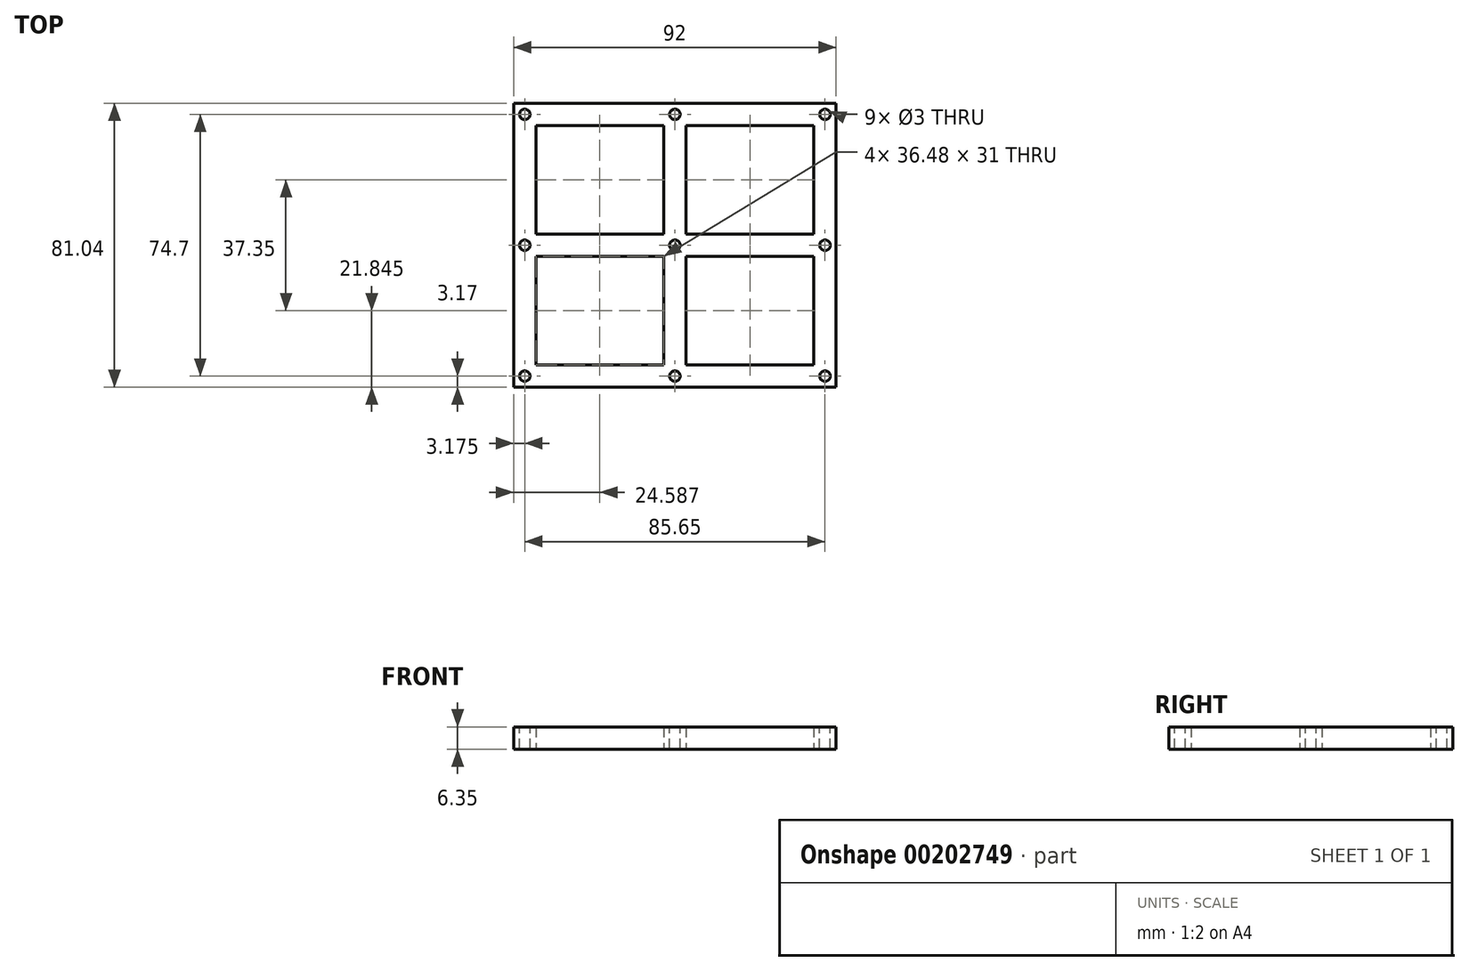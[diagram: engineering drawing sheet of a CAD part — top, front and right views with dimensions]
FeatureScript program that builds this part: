
annotation { "Feature Type Name" : "Feature", "Feature Type Description" : "" }
export const myFeature = defineFeature(function(context is Context, id is Id, definition is map)
    precondition{}
    {
        {
            var Q0;
            Q0=qCreatedBy(makeId("Top.planeOp"),FACE);
            var sketch = newSketch(context, id + "F0", { "sketchPlane" : qUnion([Q0])});
            skLineSegment(sketch, "E0.bottom", {"start": v(46, -40.52) * mm, "end": v(-46, -40.53) * mm});
            skLineSegment(sketch, "E0.top", {"start": v(46, 40.53) * mm, "end": v(-46, 40.52) * mm});
            skLineSegment(sketch, "E0.left", {"start": v(46, -40.52) * mm, "end": v(46, 40.53) * mm});
            skLineSegment(sketch, "E0.right", {"start": v(-46, -40.53) * mm, "end": v(-46, 40.52) * mm});
            skPoint(sketch, "E0.middle", {"position": v(0, 0) * mm});
            skSolve(sketch);
        }
        {
            var Q0;
            Q0 = qSketchRegion(id + "F0", true);
            extrude(context, id + "F1", {"entities" : qUnion([Q0]), "depth" : 6.35 * mm});
        }
        {
            var Q0;
            Q0=makeQuery(id+"F1.opExtrude","CAP_FACE",FACE,{"disambiguationData":[OSD([sQuery(id+"F0.wireOp",EDGE,"E0.bottom"),sQuery(id+"F0.wireOp",EDGE,"E0.top"),sQuery(id+"F0.wireOp",EDGE,"E0.left"),sQuery(id+"F0.wireOp",EDGE,"E0.right")])],"isStart":false});
            var sketch = newSketch(context, id + "F2", { "sketchPlane" : qUnion([Q0])});
            skLineSegment(sketch, "E1.bottom", {"start": v(46, 40.53) * mm, "end": v(39.65, 40.53) * mm});
            skLineSegment(sketch, "E1.top", {"start": v(46, 34.18) * mm, "end": v(39.65, 34.18) * mm});
            skLineSegment(sketch, "E1.left", {"start": v(46, 40.53) * mm, "end": v(46, 34.18) * mm});
            skLineSegment(sketch, "E1.right", {"start": v(39.65, 40.53) * mm, "end": v(39.65, 34.18) * mm});
            skLineSegment(sketch, "E2.bottom", {"start": v(-46, -40.53) * mm, "end": v(-39.65, -40.53) * mm});
            skLineSegment(sketch, "E2.top", {"start": v(-46, -34.18) * mm, "end": v(-39.65, -34.18) * mm});
            skLineSegment(sketch, "E2.left", {"start": v(-46, -40.53) * mm, "end": v(-46, -34.18) * mm});
            skLineSegment(sketch, "E2.right", {"start": v(-39.65, -40.53) * mm, "end": v(-39.65, -34.18) * mm});
            skLineSegment(sketch, "E3.bottom", {"start": v(46, -40.52) * mm, "end": v(39.65, -40.52) * mm});
            skLineSegment(sketch, "E3.top", {"start": v(46, -34.18) * mm, "end": v(39.65, -34.18) * mm});
            skLineSegment(sketch, "E3.left", {"start": v(46, -40.52) * mm, "end": v(46, -34.18) * mm});
            skLineSegment(sketch, "E3.right", {"start": v(39.65, -40.52) * mm, "end": v(39.65, -34.18) * mm});
            skLineSegment(sketch, "E4.bottom", {"start": v(46, -3.17) * mm, "end": v(39.65, -3.17) * mm});
            skLineSegment(sketch, "E4.top", {"start": v(46, 3.17) * mm, "end": v(39.65, 3.17) * mm});
            skLineSegment(sketch, "E4.left", {"start": v(46, -3.17) * mm, "end": v(46, 3.17) * mm});
            skLineSegment(sketch, "E4.right", {"start": v(-46, -3.17) * mm, "end": v(-46, 3.17) * mm});
            skPoint(sketch, "E4.middle", {"position": v(0, 0) * mm});
            skLineSegment(sketch, "E5.left", {"start": v(46, 3.17) * mm, "end": v(46, -3.17) * mm});
            skLineSegment(sketch, "E5.right", {"start": v(39.65, 3.17) * mm, "end": v(39.65, -3.17) * mm});
            skLineSegment(sketch, "E6.bottom", {"start": v(-46, 3.17) * mm, "end": v(-39.65, 3.17) * mm});
            skLineSegment(sketch, "E6.top", {"start": v(-46, -3.17) * mm, "end": v(-39.65, -3.17) * mm});
            skLineSegment(sketch, "E6.left", {"start": v(-46, 3.17) * mm, "end": v(-46, -3.17) * mm});
            skLineSegment(sketch, "E6.right", {"start": v(-39.65, 3.17) * mm, "end": v(-39.65, -3.17) * mm});
            skLineSegment(sketch, "E7.trimOffspring", {"start": v(-39.65, 3.17) * mm, "end": v(-46, 3.17) * mm});
            skLineSegment(sketch, "E8.trimOffspring", {"start": v(-39.65, -3.17) * mm, "end": v(-46, -3.17) * mm});
            skLineSegment(sketch, "E9.bottom", {"start": v(-46, 40.52) * mm, "end": v(-39.65, 40.52) * mm});
            skLineSegment(sketch, "E9.top", {"start": v(-46, 34.17) * mm, "end": v(-39.65, 34.17) * mm});
            skLineSegment(sketch, "E9.left", {"start": v(-46, 40.52) * mm, "end": v(-46, 34.17) * mm});
            skLineSegment(sketch, "E9.right", {"start": v(-39.65, 40.52) * mm, "end": v(-39.65, 34.17) * mm});
            skPoint(sketch, "E10", {"position": v(-42.83, 37.35) * mm});
            skPoint(sketch, "E10.positionSnap0", {"position": v(-46, 37.35) * mm});
            skPoint(sketch, "E10.positionSnap1", {"position": v(-42.83, 40.52) * mm});
            skPoint(sketch, "E11.positionSnap1", {"position": v(0, 40.53) * mm});
            skPoint(sketch, "E12", {"position": v(42.82, 37.35) * mm});
            skPoint(sketch, "E12.positionSnap0", {"position": v(39.65, 37.35) * mm});
            skPoint(sketch, "E12.positionSnap1", {"position": v(42.82, 40.53) * mm});
            skPoint(sketch, "E13", {"position": v(-42.83, 0) * mm});
            skPoint(sketch, "E13.positionSnap0", {"position": v(-46, 0) * mm});
            skPoint(sketch, "E13.positionSnap1", {"position": v(-42.83, 3.17) * mm});
            skPoint(sketch, "E14", {"position": v(-42.82, -37.35) * mm});
            skPoint(sketch, "E14.positionSnap0", {"position": v(-46, -37.35) * mm});
            skPoint(sketch, "E14.positionSnap1", {"position": v(-42.82, -34.18) * mm});
            skPoint(sketch, "E15", {"position": v(42.83, 0) * mm});
            skPoint(sketch, "E15.positionSnap0", {"position": v(42.83, 3.17) * mm});
            skPoint(sketch, "E15.positionSnap1", {"position": v(46, 0) * mm});
            skPoint(sketch, "E16", {"position": v(42.83, -37.35) * mm});
            skPoint(sketch, "E16.positionSnap0", {"position": v(39.65, -37.35) * mm});
            skPoint(sketch, "E16.positionSnap1", {"position": v(42.83, -34.18) * mm});
            skPoint(sketch, "E17", {"position": v(0, 37.35) * mm});
            skLineSegment(sketch, "E18.bottom", {"start": v(3.17, 40.53) * mm, "end": v(-3.18, 40.53) * mm});
            skLineSegment(sketch, "E18.top", {"start": v(3.17, 34.18) * mm, "end": v(-3.18, 34.18) * mm});
            skLineSegment(sketch, "E18.left", {"start": v(3.17, 40.53) * mm, "end": v(3.17, 34.18) * mm});
            skLineSegment(sketch, "E18.right", {"start": v(-3.18, 40.53) * mm, "end": v(-3.18, 34.18) * mm});
            skLineSegment(sketch, "E19.bottom", {"start": v(3.18, -3.17) * mm, "end": v(-3.17, -3.18) * mm});
            skLineSegment(sketch, "E19.top", {"start": v(3.17, 3.18) * mm, "end": v(-3.18, 3.17) * mm});
            skLineSegment(sketch, "E19.left", {"start": v(3.18, -3.17) * mm, "end": v(3.17, 3.18) * mm});
            skLineSegment(sketch, "E19.right", {"start": v(-3.17, -3.18) * mm, "end": v(-3.18, 3.17) * mm});
            skPoint(sketch, "E20", {"position": v(0, -37.35) * mm});
            skLineSegment(sketch, "E21.bottom", {"start": v(3.18, -40.53) * mm, "end": v(-3.17, -40.53) * mm});
            skLineSegment(sketch, "E21.top", {"start": v(3.18, -34.18) * mm, "end": v(-3.17, -34.18) * mm});
            skLineSegment(sketch, "E21.left", {"start": v(3.18, -40.53) * mm, "end": v(3.18, -34.18) * mm});
            skLineSegment(sketch, "E21.right", {"start": v(-3.17, -40.53) * mm, "end": v(-3.17, -34.18) * mm});
            skSolve(sketch);
        }
        {
            var Q0;
            Q0=makeQuery(id+"F1.opExtrude","CAP_FACE",FACE,{"disambiguationData":[OSD([sQuery(id+"F0.wireOp",EDGE,"E0.bottom"),sQuery(id+"F0.wireOp",EDGE,"E0.top"),sQuery(id+"F0.wireOp",EDGE,"E0.left"),sQuery(id+"F0.wireOp",EDGE,"E0.right")])],"isStart":true});
            var sketch = newSketch(context, id + "F3", { "sketchPlane" : qUnion([Q0])});
            skLineSegment(sketch, "E22.bottom", {"start": v(-46, 40.53) * mm, "end": v(46, 40.53) * mm});
            skLineSegment(sketch, "E22.top", {"start": v(-46, -40.53) * mm, "end": v(46, -40.53) * mm});
            skLineSegment(sketch, "E22.left", {"start": v(-46, 40.53) * mm, "end": v(-46, -40.52) * mm});
            skLineSegment(sketch, "E22.right", {"start": v(46, 40.52) * mm, "end": v(46, -40.53) * mm});
            skLineSegment(sketch, "E23.top", {"start": v(-39.65, 34.18) * mm, "end": v(-3.17, 34.18) * mm});
            skLineSegment(sketch, "E23.right", {"start": v(46, 40.53) * mm, "end": v(46, 34.18) * mm});
            skLineSegment(sketch, "E24.top", {"start": v(-39.65, -34.17) * mm, "end": v(39.65, -34.17) * mm});
            skLineSegment(sketch, "E24.left", {"start": v(-46, -40.52) * mm, "end": v(-46, -34.17) * mm});
            skLineSegment(sketch, "E24.right", {"start": v(46, -40.53) * mm, "end": v(46, -34.17) * mm});
            skLineSegment(sketch, "E25.top", {"start": v(-46, -40.52) * mm, "end": v(-39.65, -40.52) * mm});
            skLineSegment(sketch, "E25.right", {"start": v(-39.65, 34.18) * mm, "end": v(-39.65, 3.17) * mm});
            skLineSegment(sketch, "E26.bottom", {"start": v(46, 40.53) * mm, "end": v(39.65, 40.53) * mm});
            skLineSegment(sketch, "E26.top", {"start": v(46, -40.53) * mm, "end": v(39.65, -40.53) * mm});
            skLineSegment(sketch, "E26.right", {"start": v(39.65, 34.18) * mm, "end": v(39.65, 3.17) * mm});
            skLineSegment(sketch, "E27.bottom", {"start": v(39.65, -3.18) * mm, "end": v(3.18, -3.18) * mm});
            skLineSegment(sketch, "E27.top", {"start": v(39.65, 3.17) * mm, "end": v(3.18, 3.17) * mm});
            skLineSegment(sketch, "E27.left", {"start": v(46, -3.18) * mm, "end": v(46, 3.17) * mm});
            skLineSegment(sketch, "E27.right", {"start": v(-46, -3.18) * mm, "end": v(-46, 3.17) * mm});
            skPoint(sketch, "E27.middle", {"position": v(0, 0) * mm});
            skLineSegment(sketch, "E28.bottom", {"start": v(3.18, 40.53) * mm, "end": v(-3.17, 40.53) * mm});
            skLineSegment(sketch, "E28.top", {"start": v(3.18, -40.53) * mm, "end": v(-3.17, -40.53) * mm});
            skLineSegment(sketch, "E28.left", {"start": v(3.18, 34.18) * mm, "end": v(3.18, 3.17) * mm});
            skLineSegment(sketch, "E28.right", {"start": v(-3.17, 34.18) * mm, "end": v(-3.17, 3.17) * mm});
            skPoint(sketch, "E29.orphan", {"position": v(-46, 34.18) * mm});
            skPoint(sketch, "E30.orphan", {"position": v(-39.65, 40.53) * mm});
            skLineSegment(sketch, "E31.trimOffspring", {"start": v(3.18, 34.18) * mm, "end": v(39.65, 34.18) * mm});
            skLineSegment(sketch, "E32.trimOffspring", {"start": v(-3.17, 3.17) * mm, "end": v(-39.65, 3.17) * mm});
            skLineSegment(sketch, "E33.trimOffspring", {"start": v(-3.17, -3.18) * mm, "end": v(-39.65, -3.18) * mm});
            skLineSegment(sketch, "E34.trimOffspring", {"start": v(-3.17, -3.18) * mm, "end": v(-3.17, -34.17) * mm});
            skLineSegment(sketch, "E35.trimOffspring", {"start": v(-39.65, -3.18) * mm, "end": v(-39.65, -34.17) * mm});
            skLineSegment(sketch, "E36.trimOffspring", {"start": v(3.18, -3.18) * mm, "end": v(3.18, -34.17) * mm});
            skLineSegment(sketch, "E37.trimOffspring", {"start": v(39.65, -3.18) * mm, "end": v(39.65, -34.17) * mm});
            skLineSegment(sketch, "E38.bottom", {"start": v(-46, 40.53) * mm, "end": v(-39.65, 40.53) * mm});
            skLineSegment(sketch, "E38.top", {"start": v(-46, 34.18) * mm, "end": v(-39.65, 34.18) * mm});
            skLineSegment(sketch, "E38.left", {"start": v(-46, 40.53) * mm, "end": v(-46, 34.18) * mm});
            skLineSegment(sketch, "E38.right", {"start": v(-39.65, 40.53) * mm, "end": v(-39.65, 34.18) * mm});
            skLineSegment(sketch, "E39.top", {"start": v(46, 34.18) * mm, "end": v(39.65, 34.18) * mm});
            skLineSegment(sketch, "E39.left", {"start": v(46, 40.52) * mm, "end": v(46, 34.18) * mm});
            skLineSegment(sketch, "E39.right", {"start": v(39.65, 40.53) * mm, "end": v(39.65, 34.18) * mm});
            skLineSegment(sketch, "E40.bottom", {"start": v(-3.17, 40.53) * mm, "end": v(3.18, 40.53) * mm});
            skLineSegment(sketch, "E40.top", {"start": v(-3.17, 34.18) * mm, "end": v(3.18, 34.18) * mm});
            skLineSegment(sketch, "E40.left", {"start": v(-3.17, 40.53) * mm, "end": v(-3.17, 34.18) * mm});
            skLineSegment(sketch, "E40.right", {"start": v(3.18, 40.53) * mm, "end": v(3.18, 34.18) * mm});
            skLineSegment(sketch, "E41.bottom", {"start": v(-46, 3.17) * mm, "end": v(-39.65, 3.17) * mm});
            skLineSegment(sketch, "E41.top", {"start": v(-46, -3.18) * mm, "end": v(-39.65, -3.18) * mm});
            skLineSegment(sketch, "E41.left", {"start": v(-46, 3.17) * mm, "end": v(-46, -3.18) * mm});
            skLineSegment(sketch, "E41.right", {"start": v(-39.65, 3.17) * mm, "end": v(-39.65, -3.18) * mm});
            skLineSegment(sketch, "E42.bottom", {"start": v(-3.17, 3.17) * mm, "end": v(3.18, 3.17) * mm});
            skLineSegment(sketch, "E42.top", {"start": v(-3.17, -3.18) * mm, "end": v(3.18, -3.18) * mm});
            skLineSegment(sketch, "E42.left", {"start": v(-3.17, 3.17) * mm, "end": v(-3.17, -3.18) * mm});
            skLineSegment(sketch, "E42.right", {"start": v(3.18, 3.17) * mm, "end": v(3.18, -3.18) * mm});
            skLineSegment(sketch, "E43.bottom", {"start": v(46, 3.17) * mm, "end": v(39.65, 3.17) * mm});
            skLineSegment(sketch, "E43.top", {"start": v(46, -3.18) * mm, "end": v(39.65, -3.18) * mm});
            skLineSegment(sketch, "E43.left", {"start": v(46, 3.17) * mm, "end": v(46, -3.18) * mm});
            skLineSegment(sketch, "E43.right", {"start": v(39.65, 3.17) * mm, "end": v(39.65, -3.18) * mm});
            skLineSegment(sketch, "E44.bottom", {"start": v(-46, -34.17) * mm, "end": v(-39.65, -34.17) * mm});
            skLineSegment(sketch, "E44.left", {"start": v(-46, -34.17) * mm, "end": v(-46, -40.52) * mm});
            skLineSegment(sketch, "E44.right", {"start": v(-39.65, -34.17) * mm, "end": v(-39.65, -40.52) * mm});
            skLineSegment(sketch, "E45.bottom", {"start": v(-3.17, -34.17) * mm, "end": v(3.18, -34.17) * mm});
            skLineSegment(sketch, "E45.top", {"start": v(-3.17, -40.53) * mm, "end": v(3.18, -40.53) * mm});
            skLineSegment(sketch, "E45.left", {"start": v(-3.17, -34.17) * mm, "end": v(-3.17, -40.53) * mm});
            skLineSegment(sketch, "E45.right", {"start": v(3.18, -34.17) * mm, "end": v(3.18, -40.53) * mm});
            skLineSegment(sketch, "E46.bottom", {"start": v(39.65, -34.17) * mm, "end": v(46, -34.17) * mm});
            skLineSegment(sketch, "E46.top", {"start": v(39.65, -40.53) * mm, "end": v(46, -40.53) * mm});
            skLineSegment(sketch, "E46.left", {"start": v(39.65, -34.17) * mm, "end": v(39.65, -40.53) * mm});
            skLineSegment(sketch, "E46.right", {"start": v(46, -34.17) * mm, "end": v(46, -40.53) * mm});
            skPoint(sketch, "E47", {"position": v(-42.82, 37.35) * mm});
            skPoint(sketch, "E47.positionSnap0", {"position": v(-46, 37.35) * mm});
            skPoint(sketch, "E47.positionSnap1", {"position": v(-42.82, 40.53) * mm});
            skPoint(sketch, "E48", {"position": v(0, 37.35) * mm});
            skPoint(sketch, "E48.positionSnap0", {"position": v(-3.17, 37.35) * mm});
            skPoint(sketch, "E48.positionSnap1", {"position": v(0, 40.53) * mm});
            skPoint(sketch, "E49", {"position": v(42.83, 37.35) * mm});
            skPoint(sketch, "E49.positionSnap0", {"position": v(39.65, 37.35) * mm});
            skPoint(sketch, "E49.positionSnap1", {"position": v(42.83, 40.53) * mm});
            skPoint(sketch, "E50", {"position": v(-42.82, 0) * mm});
            skPoint(sketch, "E50.positionSnap0", {"position": v(-46, 0) * mm});
            skPoint(sketch, "E50.positionSnap1", {"position": v(-42.82, 3.17) * mm});
            skPoint(sketch, "E51", {"position": v(42.83, 0) * mm});
            skPoint(sketch, "E51.positionSnap0", {"position": v(42.83, 3.17) * mm});
            skPoint(sketch, "E51.positionSnap1", {"position": v(39.65, 0) * mm});
            skPoint(sketch, "E52", {"position": v(42.83, -37.35) * mm});
            skPoint(sketch, "E52.positionSnap0", {"position": v(39.65, -37.35) * mm});
            skPoint(sketch, "E52.positionSnap1", {"position": v(42.83, -34.17) * mm});
            skPoint(sketch, "E53", {"position": v(0, -37.35) * mm});
            skPoint(sketch, "E53.positionSnap0", {"position": v(-3.17, -37.35) * mm});
            skPoint(sketch, "E53.positionSnap1", {"position": v(0, -34.17) * mm});
            skPoint(sketch, "E54", {"position": v(-42.83, -37.35) * mm});
            skPoint(sketch, "E54.positionSnap0", {"position": v(-42.83, -34.17) * mm});
            skPoint(sketch, "E54.positionSnap1", {"position": v(-46, -37.35) * mm});
            skPoint(sketch, "E55", {"position": v(0, -30.28) * mm});
            skSolve(sketch);
        }
        {
            var Q0;
            Q0=makeQuery(id+"F3.imprint","IMPRINT",FACE,{"disambiguationData":[TD([[makeQuery(id+"F3.imprint","IMPRINT",EDGE,{"derivedFrom":sQuery(id+"F3.wireOp",EDGE,"E23.top")}),-1.0]])]});
            var Q1;
            Q1=makeQuery(id+"F3.imprint","IMPRINT",FACE,{"disambiguationData":[TD([[makeQuery(id+"F3.imprint","IMPRINT",EDGE,{"derivedFrom":sQuery(id+"F3.wireOp",EDGE,"E33.trimOffspring")}),1.0]])]});
            var Q2;
            Q2=makeQuery(id+"F3.imprint","IMPRINT",FACE,{"disambiguationData":[TD([[makeQuery(id+"F3.imprint","IMPRINT",EDGE,{"derivedFrom":sQuery(id+"F3.wireOp",EDGE,"E26.right")}),-1.0]])]});
            var Q3;
            Q3=makeQuery(id+"F3.imprint","IMPRINT",FACE,{"disambiguationData":[TD([[makeQuery(id+"F3.imprint","IMPRINT",EDGE,{"derivedFrom":sQuery(id+"F3.wireOp",EDGE,"E27.bottom")}),1.0]])]});
            extrude(context, id + "F4", {"entities" : qUnion([Q0, Q1, Q2, Q3]), "operationType" : NewBodyOperationType.REMOVE, "oppositeDirection" : true, "depth" : 6.35 * mm});
        }
        {
            var Q0;
            Q0=sQuery(id+"F2.wireOp",VERTEX,"E10");
            var Q1;
            Q1=sQuery(id+"F2.wireOp",VERTEX,"E17");
            var Q2;
            Q2=sQuery(id+"F2.wireOp",VERTEX,"E12");
            var Q3;
            Q3=sQuery(id+"F2.wireOp",VERTEX,"E13");
            var Q4;
            Q4=sQuery(id+"F2.wireOp",VERTEX,"E4.middle");
            var Q5;
            Q5=sQuery(id+"F2.wireOp",VERTEX,"E15");
            var Q6;
            Q6=sQuery(id+"F2.wireOp",VERTEX,"E14");
            var Q7;
            Q7=sQuery(id+"F2.wireOp",VERTEX,"E20");
            var Q8;
            Q8=sQuery(id+"F2.wireOp",VERTEX,"E16");
            var Q9;
            Q9=makeQuery(id+"F1.opExtrude","SWEPT_BODY",BODY,{"disambiguationData":[OSD([sQuery(id+"F0.wireOp",EDGE,"E0.bottom"),sQuery(id+"F0.wireOp",EDGE,"E0.top"),sQuery(id+"F0.wireOp",EDGE,"E0.left"),sQuery(id+"F0.wireOp",EDGE,"E0.right")])]});
            hole(context, id + "F5", {"style" : HoleStyle.SIMPLE, "endStyle" : HoleEndStyle.THROUGH, "standardTappedOrClearance" : lookupTablePath({ "standard" : "ISO", "size" : "3", "type" : "Drilled" }), "standardBlindInLast" : lookupTablePath({ "standard" : "ISO", "size" : "3", "type" : "Drilled" }), "holeDiameter" : 3 * mm, "startFromSketch" : true, "locations" : qUnion([Q0, Q1, Q2, Q3, Q4, Q5, Q6, Q7, Q8]), "scope" : qUnion([Q9]), "isTappedThrough" : true});
        }
    });
